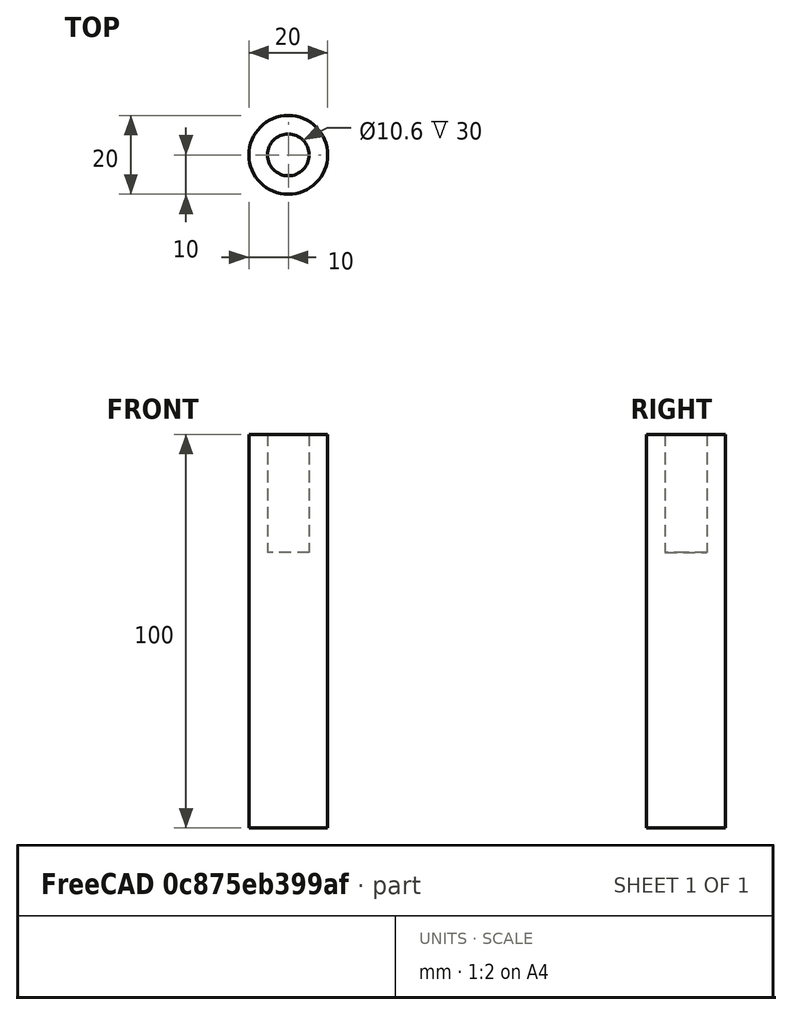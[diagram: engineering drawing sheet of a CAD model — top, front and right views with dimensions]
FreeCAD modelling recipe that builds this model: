
FCSTD DOCUMENT  (FreeCAD 0.16R)
Label: pillar
License: All rights reserved
LicenseURL: http://en.wikipedia.org/wiki/All_rights_reserved
objects: Sketcher::SketchObject×1, PartDesign::Revolution×1
note: 3 computed .brp shape members not serialized (recipe doc carries the construction recipe); baked Part::Feature solids carry a one-line shape summary decoded from their .brp

FEATURE [Sketcher::SketchObject] Sketch
  Placement = pos=(0,0,0) rot=(-1,0,0;4.71239rad)
  sketch-geometry (6):
    g0: LineSegment StartX=0 StartY=70 StartZ=0 EndX=0 EndY=0 EndZ=0
    g1: LineSegment StartX=0 StartY=0 StartZ=0 EndX=10 EndY=0 EndZ=0
    g2: LineSegment StartX=10 StartY=0 StartZ=0 EndX=10 EndY=100 EndZ=0
    g3: LineSegment StartX=10 StartY=100 StartZ=0 EndX=5.3 EndY=100 EndZ=0
    g4: LineSegment StartX=5.3 StartY=100 StartZ=0 EndX=5.3 EndY=70 EndZ=0
    g5: LineSegment StartX=5.3 StartY=70 StartZ=0 EndX=0 EndY=70 EndZ=0
  constraints (17):
    c: Coincident(g0,g-1)
    c: Vertical(g0)
    c: Coincident(g0,g1)
    c: Horizontal(g1)
    c: Coincident(g1,g2)
    c: Vertical(g2)
    c: Coincident(g2,g3)
    c: Coincident(g3,g4)
    c: Vertical(g4)
    c: Coincident(g4,g5)
    c: Coincident(g5,g0)
    c: Parallel(g5,g1)
    c: Parallel(g3,g1)
    c: DistanceY(g2,g2) = 100
    c: DistanceX(g1,g1) = 10
    c: DistanceY(g4,g4) = 30
    c: DistanceX(g5,g5) = 5.3
FEATURE [PartDesign::Revolution] Revolution
  Angle = 360
  Axis = (0,0,1)
  Base = (0,0,0)
  Placement = pos=(0,0,0) rot=(-1,0,0;4.71239rad)
  ReferenceAxis = -> Sketch [V_Axis]
  Reversed = true
  Sketch = -> Sketch
